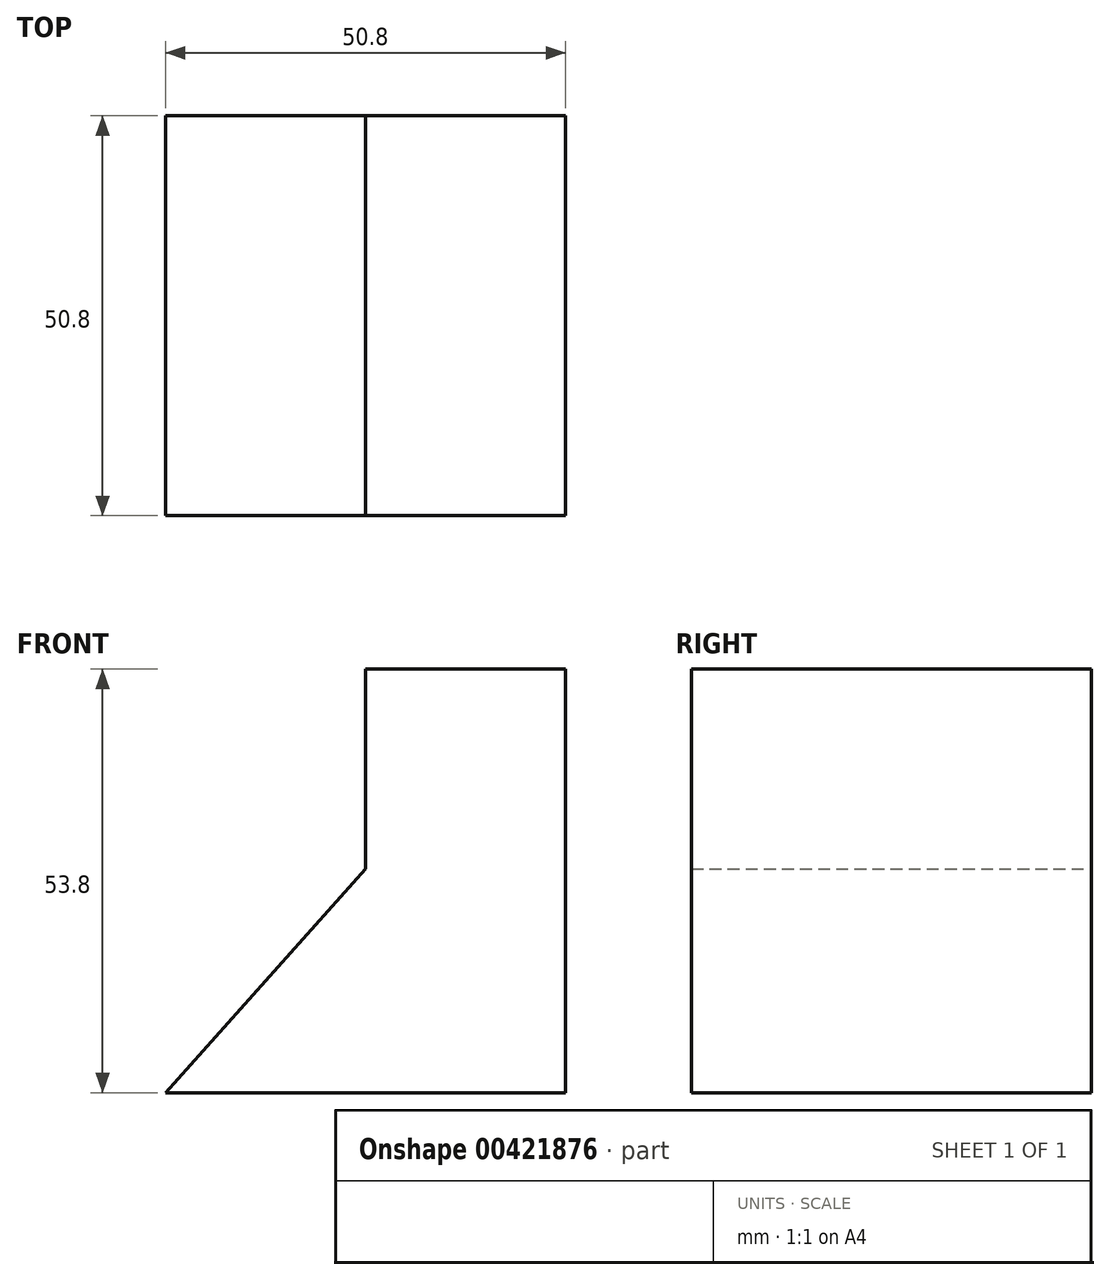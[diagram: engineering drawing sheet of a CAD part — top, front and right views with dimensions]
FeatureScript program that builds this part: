
annotation { "Feature Type Name" : "Feature", "Feature Type Description" : "" }
export const myFeature = defineFeature(function(context is Context, id is Id, definition is map)
    precondition{}
    {
        {
            var Q0;
            Q0=qCreatedBy(makeId("Front.planeOp"),FACE);
            var sketch = newSketch(context, id + "F0", { "sketchPlane" : qUnion([Q0])});
            skLineSegment(sketch, "E0", {"start": v(0, 0) * mm, "end": v(-50.8, 0) * mm});
            skLineSegment(sketch, "E1", {"start": v(-50.8, 0) * mm, "end": v(-25.4, 28.4) * mm});
            skLineSegment(sketch, "E2", {"start": v(-25.4, 28.4) * mm, "end": v(-25.4, 53.8) * mm});
            skLineSegment(sketch, "E3", {"start": v(-25.4, 53.8) * mm, "end": v(0, 53.8) * mm});
            skLineSegment(sketch, "E4", {"start": v(0, 53.8) * mm, "end": v(0, 0) * mm});
            skSolve(sketch);
        }
        {
            var Q0;
            Q0 = qSketchRegion(id + "F0", true);
            extrude(context, id + "F1", {"entities" : qUnion([Q0]), "depth" : 50.8 * mm});
        }
    });
